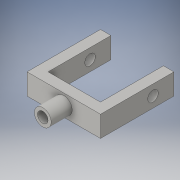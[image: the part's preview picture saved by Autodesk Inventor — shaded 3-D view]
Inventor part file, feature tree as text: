
AUTODESK INVENTOR PART (.ipt)
format: ipt  version: 2016 (Build 200138000, 138)  size: 124,928 bytes
history: native  units: in
note: dims shown in document units (in); Inventor stores cm internally (conversion verified against a paired STEP export)
features: extrude x3, sketch x3
ambient origin geometry x8: Origin, YZ Plane, XZ Plane, XY Plane, X Axis, Y Axis, Z Axis, Center Point
bodies: Solid1 (feature_tree)
feature tree (6):
  extrude  "Extrusion1"  Depth=0.4921in
  extrude  "Extrusion2"  Depth=1.1811in
  extrude  "Extrusion3"  Depth=1.378in
  sketch  "Sketch1"  dims[d0=0.4921in d1=0.4921in]
  sketch  "Sketch2"  dims[d2=1.1811in d3=1.1811in]
  sketch  "Sketch3"  dims[d4=0.1969in d5=1.378in d6=0.1969in d7=1.378in d8=0.3937in d9=0.0in d10=0.3937in d11=0.1969in d12=1.378in d13=0.0in d14=0.315in d15=0.1969in d16=0.3937in d17=0.0in]
